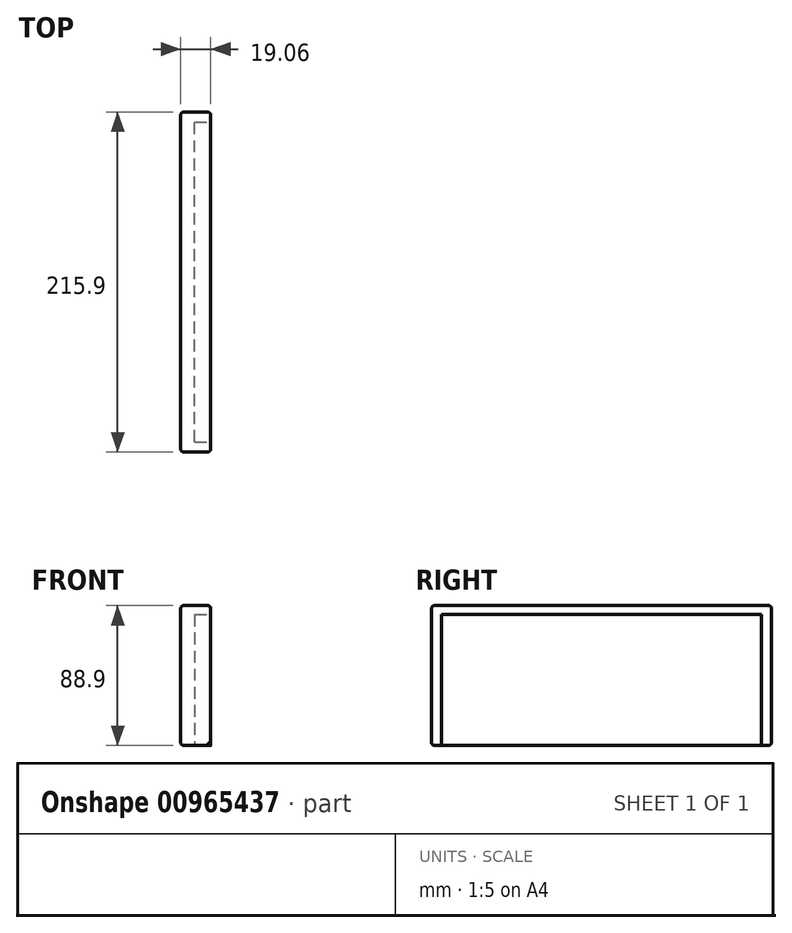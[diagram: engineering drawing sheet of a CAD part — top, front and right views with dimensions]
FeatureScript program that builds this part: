
annotation { "Feature Type Name" : "Feature", "Feature Type Description" : "" }
export const myFeature = defineFeature(function(context is Context, id is Id, definition is map)
    precondition{}
    {
        {
            var Q0;
            Q0=qCreatedBy(makeId("Top.planeOp"),FACE);
            var sketch = newSketch(context, id + "F0", { "sketchPlane" : qUnion([Q0])});
            skLineSegment(sketch, "E0.bottom", {"start": v(9.53, -107.95) * mm, "end": v(-9.52, -107.95) * mm});
            skLineSegment(sketch, "E0.top", {"start": v(9.52, 107.95) * mm, "end": v(-9.53, 107.95) * mm});
            skLineSegment(sketch, "E0.left", {"start": v(9.53, -107.95) * mm, "end": v(9.52, 107.95) * mm});
            skLineSegment(sketch, "E0.right", {"start": v(-9.52, -107.95) * mm, "end": v(-9.53, 107.95) * mm});
            skPoint(sketch, "E0.middle", {"position": v(0, 0) * mm});
            skSolve(sketch);
        }
        {
            var Q0;
            {var subQ4=sQuery(id+"F0.wireOp",EDGE,"E0.bottom");Q0=makeQuery(id+"F0.imprint","IMPRINT",FACE,{"disambiguationData":[TD([[makeQuery(id+"F0.imprint","IMPRINT",EDGE,{"derivedFrom":subQ4}),-1.0]])]});}
            var Q1;
            Q1=makeQuery(id+"F0.imprint","IMPRINT",FACE,{"disambiguationData":[TD([[makeQuery(id+"F0.imprint","IMPRINT",EDGE,{"derivedFrom":sQuery(id+"F0.wireOp",EDGE,"CqbxAs32-swxf-Njvs-v4lD-9BbbaOkjSHAn.bottom")}),-1.0]])]});
            var Q2;
            Q2=sQuery(id+"F0.wireOp",EDGE,"E0.right");
            var Q3;
            Q3=sQuery(id+"F0.wireOp",EDGE,"E0.top");
            var Q4;
            Q4=sQuery(id+"F0.wireOp",EDGE,"E0.left");
            var Q5;
            Q5=sQuery(id+"F0.wireOp",EDGE,"E0.bottom");
            extrude(context, id + "F1", {"entities" : qUnion([Q0, Q1]), "surfaceEntities" : qUnion([Q2, Q3, Q4, Q5]), "depth" : 88.9 * mm, "offsetDistance" : 25 * mm});
        }
        {
            var Q0;
            Q0=makeQuery(id+"F1.opExtrude","SWEPT_FACE",FACE,{"disambiguationData":[OSD([sQuery(id+"F0.wireOp",EDGE,"E0.left")])]});
            var sketch = newSketch(context, id + "F2", { "sketchPlane" : qUnion([Q0])});
            skLineSegment(sketch, "E1.bottom", {"start": v(-101.6, 83.2) * mm, "end": v(101.6, 83.2) * mm});
            skLineSegment(sketch, "E1.top", {"start": v(-101.6, 0) * mm, "end": v(101.6, 0) * mm});
            skLineSegment(sketch, "E1.left", {"start": v(-101.6, 83.2) * mm, "end": v(-101.6, 0) * mm});
            skLineSegment(sketch, "E1.right", {"start": v(101.6, 83.2) * mm, "end": v(101.6, 0) * mm});
            skLineSegment(sketch, "E2", {"start": v(0, 88.9) * mm, "end": v(0, -17.95) * mm, "construction": true});
            skSolve(sketch);
        }
        {
            var Q0;
            Q0 = qSketchRegion(id + "F2", true);
            extrude(context, id + "F3", {"entities" : qUnion([Q0]), "operationType" : NewBodyOperationType.REMOVE, "oppositeDirection" : true, "depth" : 10.16 * mm, "offsetDistance" : 25 * mm});
        }
        {
            var Q0;
            Q0=makeQuery(id+"F1.opExtrude","CAP_EDGE",EDGE,{"disambiguationData":[OSD([sQuery(id+"F0.wireOp",EDGE,"E0.right")])],"isStart":false});
            var Q1;
            Q1=makeQuery(id+"F1.opExtrude","CAP_EDGE",EDGE,{"disambiguationData":[OSD([sQuery(id+"F0.wireOp",EDGE,"E0.bottom")])],"isStart":false});
            var Q2;
            Q2=makeQuery(id+"F1.opExtrude","SWEPT_EDGE",EDGE,{"disambiguationData":[OSD([sQuery(id+"F0.wireOp",EDGE,"E0.bottom"),sQuery(id+"F0.wireOp",EDGE,"E0.right")])]});
            var Q3;
            Q3=makeQuery(id+"F1.opExtrude","SWEPT_EDGE",EDGE,{"disambiguationData":[OSD([sQuery(id+"F0.wireOp",EDGE,"E0.top"),sQuery(id+"F0.wireOp",EDGE,"E0.right")])]});
            var Q4;
            Q4=makeQuery(id+"F1.opExtrude","CAP_EDGE",EDGE,{"disambiguationData":[OSD([sQuery(id+"F0.wireOp",EDGE,"E0.top")])],"isStart":false});
            var Q5;
            Q5=makeQuery(id+"F1.opExtrude","CAP_EDGE",EDGE,{"disambiguationData":[OSD([sQuery(id+"F0.wireOp",EDGE,"E0.left")])],"isStart":false});
            var Q6;
            Q6=makeQuery(id+"F1.opExtrude","SWEPT_EDGE",EDGE,{"disambiguationData":[OSD([sQuery(id+"F0.wireOp",EDGE,"E0.bottom"),sQuery(id+"F0.wireOp",EDGE,"E0.left")])]});
            var Q7;
            Q7=makeQuery(id+"F1.opExtrude","SWEPT_EDGE",EDGE,{"disambiguationData":[OSD([sQuery(id+"F0.wireOp",EDGE,"E0.top"),sQuery(id+"F0.wireOp",EDGE,"E0.left")])]});
            var Q8;
            Q8=makeQuery(id+"F1.opExtrude","CAP_EDGE",EDGE,{"disambiguationData":[OSD([sQuery(id+"F0.wireOp",EDGE,"E0.right")])],"isStart":true});
            var Q9;
            Q9=makeQuery(id+"F1.opExtrude","CAP_EDGE",EDGE,{"disambiguationData":[OSD([sQuery(id+"F0.wireOp",EDGE,"E0.top")])],"isStart":true});
            var Q10;
            Q10=makeQuery(id+"F1.opExtrude","CAP_EDGE",EDGE,{"disambiguationData":[OSD([sQuery(id+"F0.wireOp",EDGE,"E0.bottom")])],"isStart":true});
            fillet(context, id + "F4", {"entities" : qUnion([Q0, Q1, Q2, Q3, Q4, Q5, Q6, Q7, Q8, Q9, Q10]), "radius" : 2 * mm, "tangentPropagation" : true, "allowEdgeOverflow" : false});
        }
    });
